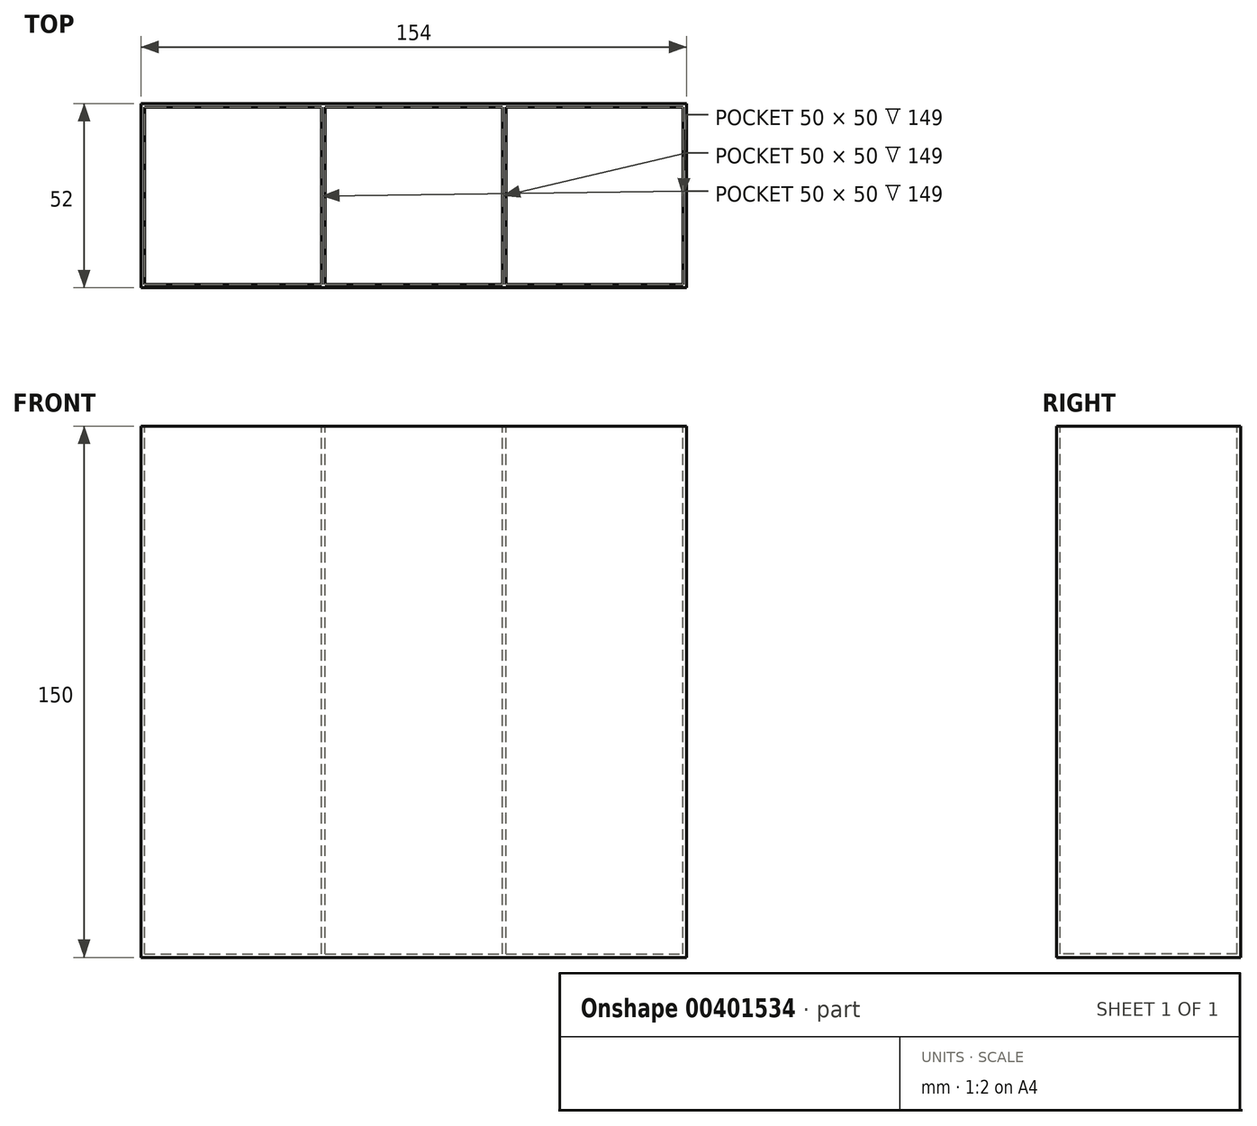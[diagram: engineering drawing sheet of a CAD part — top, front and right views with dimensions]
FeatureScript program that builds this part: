
annotation { "Feature Type Name" : "Feature", "Feature Type Description" : "" }
export const myFeature = defineFeature(function(context is Context, id is Id, definition is map)
    precondition{}
    {
        {
            var Q0;
            Q0=qCreatedBy(makeId("Top.planeOp"),FACE);
            var sketch = newSketch(context, id + "F0", { "sketchPlane" : qUnion([Q0])});
            skLineSegment(sketch, "E0.bottom", {"start": v(77, 26) * mm, "end": v(-77, 26) * mm});
            skLineSegment(sketch, "E0.top", {"start": v(77, -26) * mm, "end": v(-77, -26) * mm});
            skLineSegment(sketch, "E0.left", {"start": v(77, 26) * mm, "end": v(77, -26) * mm});
            skLineSegment(sketch, "E0.right", {"start": v(-77, 26) * mm, "end": v(-77, -26) * mm});
            skPoint(sketch, "E0.middle", {"position": v(0, 0) * mm});
            skSolve(sketch);
        }
        {
            var Q0;
            Q0=makeQuery(id+"F0.imprint","IMPRINT",FACE,{"disambiguationData":[TD([[makeQuery(id+"F0.imprint","IMPRINT",EDGE,{"derivedFrom":sQuery(id+"F0.wireOp",EDGE,"E0.bottom")}),1.0]])]});
            extrude(context, id + "F1", {"entities" : qUnion([Q0]), "depth" : 150 * mm});
        }
        {
            var Q0;
            Q0=makeQuery(id+"F1.opExtrude","CAP_FACE",FACE,{"disambiguationData":[OSD([sQuery(id+"F0.wireOp",EDGE,"E0.bottom"),sQuery(id+"F0.wireOp",EDGE,"E0.top"),sQuery(id+"F0.wireOp",EDGE,"E0.left"),sQuery(id+"F0.wireOp",EDGE,"E0.right")])],"isStart":false});
            var sketch = newSketch(context, id + "F2", { "sketchPlane" : qUnion([Q0])});
            skLineSegment(sketch, "E1.bottom", {"start": v(-76, 25) * mm, "end": v(-26, 25) * mm});
            skLineSegment(sketch, "E1.top", {"start": v(-76, -25) * mm, "end": v(-26, -25) * mm});
            skLineSegment(sketch, "E1.left", {"start": v(-76, 25) * mm, "end": v(-76, -25) * mm});
            skLineSegment(sketch, "E1.right", {"start": v(-26, 25) * mm, "end": v(-26, -25) * mm});
            skLineSegment(sketch, "E2.1.0.0", {"start": v(25, 25) * mm, "end": v(25, -25) * mm});
            skLineSegment(sketch, "E2.1.0.1", {"start": v(-25, 25) * mm, "end": v(25, 25) * mm});
            skLineSegment(sketch, "E2.1.0.2", {"start": v(-25, 25) * mm, "end": v(-25, -25) * mm});
            skLineSegment(sketch, "E2.1.0.3", {"start": v(-25, -25) * mm, "end": v(25, -25) * mm});
            skLineSegment(sketch, "E2.2.0.0", {"start": v(76, 25) * mm, "end": v(76, -25) * mm});
            skLineSegment(sketch, "E2.2.0.1", {"start": v(26, 25) * mm, "end": v(76, 25) * mm});
            skLineSegment(sketch, "E2.2.0.2", {"start": v(26, 25) * mm, "end": v(26, -25) * mm});
            skLineSegment(sketch, "E2.2.0.3", {"start": v(26, -25) * mm, "end": v(76, -25) * mm});
            skLineSegment(sketch, "E2.direction1", {"start": v(-26, -25) * mm, "end": v(25, -25) * mm, "construction": true});
            skSolve(sketch);
        }
        {
            var Q0;
            Q0=makeQuery(id+"F2.imprint","IMPRINT",FACE,{"disambiguationData":[TD([[makeQuery(id+"F2.imprint","IMPRINT",EDGE,{"derivedFrom":sQuery(id+"F2.wireOp",EDGE,"E1.bottom")}),-1.0]])]});
            var Q1;
            Q1=makeQuery(id+"F2.imprint","IMPRINT",FACE,{"disambiguationData":[TD([[makeQuery(id+"F2.imprint","IMPRINT",EDGE,{"derivedFrom":sQuery(id+"F2.wireOp",EDGE,"E2.1.0.0")}),-1.0]])]});
            var Q2;
            Q2=makeQuery(id+"F2.imprint","IMPRINT",FACE,{"disambiguationData":[TD([[makeQuery(id+"F2.imprint","IMPRINT",EDGE,{"derivedFrom":sQuery(id+"F2.wireOp",EDGE,"E2.2.0.0")}),-1.0]])]});
            extrude(context, id + "F3", {"entities" : qUnion([Q0, Q1, Q2]), "operationType" : NewBodyOperationType.REMOVE, "oppositeDirection" : true, "depth" : 149 * mm});
        }
    });
